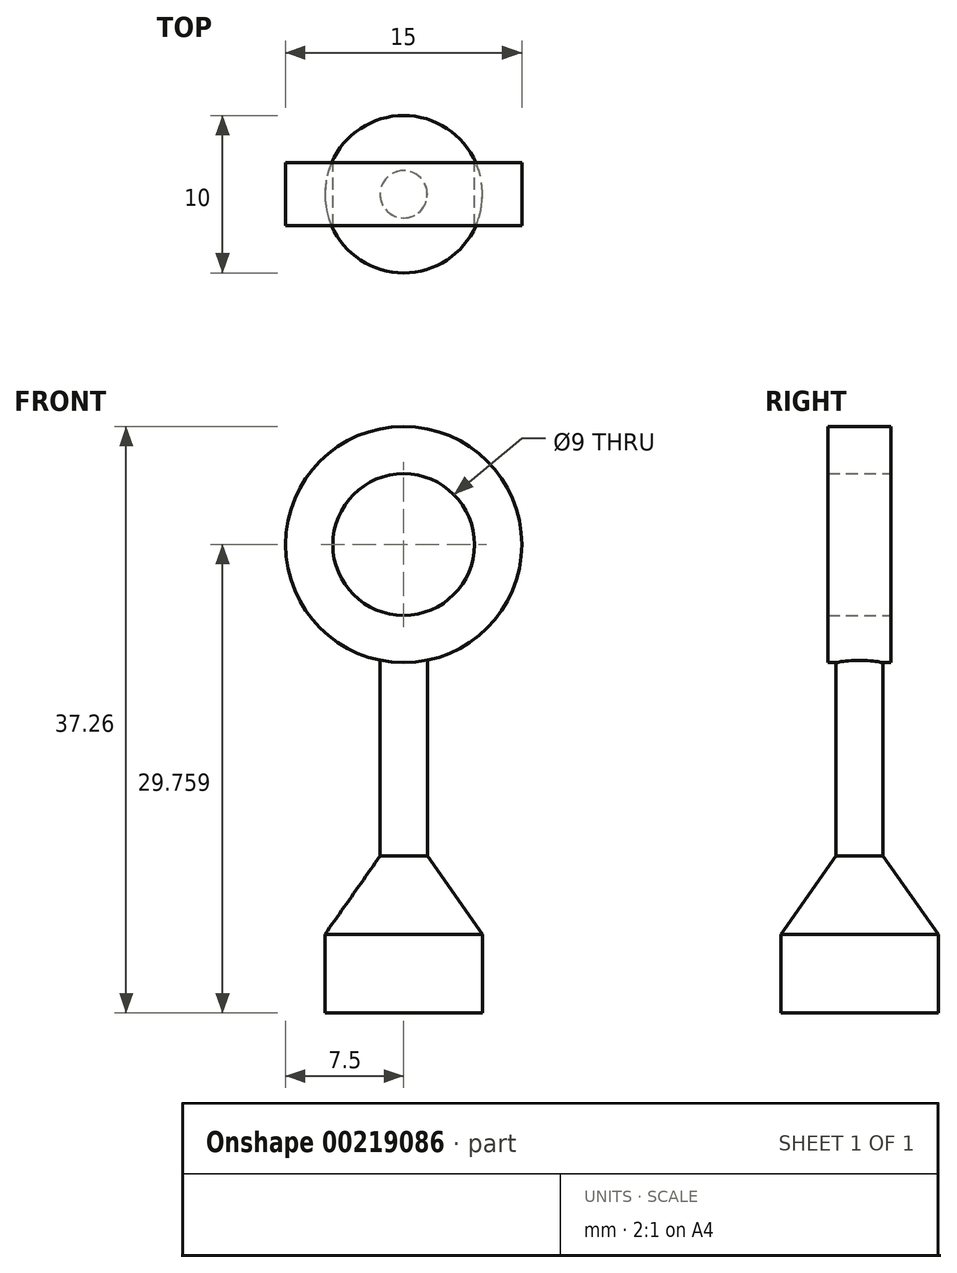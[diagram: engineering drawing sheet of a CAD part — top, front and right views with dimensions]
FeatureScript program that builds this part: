
annotation { "Feature Type Name" : "Feature", "Feature Type Description" : "" }
export const myFeature = defineFeature(function(context is Context, id is Id, definition is map)
    precondition{}
    {
        {
            var Q0;
            Q0=qCreatedBy(makeId("Top.planeOp"),FACE);
            var sketch = newSketch(context, id + "F0", { "sketchPlane" : qUnion([Q0])});
            skCircle(sketch, "E0", {"center": v(0, 0) * mm, "radius": 5 * mm});
            skSolve(sketch);
        }
        {
            var Q0;
            Q0=makeQuery(id+"F0.imprint","IMPRINT",FACE,{"disambiguationData":[TD([[makeQuery(id+"F0.imprint","IMPRINT",EDGE,{"derivedFrom":sQuery(id+"F0.wireOp",EDGE,"E0")}),1.0]])]});
            extrude(context, id + "F1", {"entities" : qUnion([Q0]), "depth" : 5 * mm});
        }
        {
            var Q0;
            Q0=makeQuery(id+"F1.opExtrude","CAP_FACE",FACE,{"disambiguationData":[OSD([sQuery(id+"F0.wireOp",EDGE,"E0")])],"isStart":false});
            var sketch = newSketch(context, id + "F2", { "sketchPlane" : qUnion([Q0])});
            skCircle(sketch, "E1", {"center": v(0, 0) * mm, "radius": 1.5 * mm});
            skSolve(sketch);
        }
        {
            var Q0;
            Q0=qCreatedBy(makeId("Front.planeOp"),FACE);
            var sketch = newSketch(context, id + "F3", { "sketchPlane" : qUnion([Q0])});
            skCircle(sketch, "E2", {"center": v(0, 29.76) * mm, "radius": 7.5 * mm});
            skCircle(sketch, "E3.0", {"center": v(0, 29.76) * mm, "radius": 4.5 * mm});
            skLineSegment(sketch, "E4", {"start": v(0, 12.11) * mm, "end": v(5, 5) * mm});
            skLineSegment(sketch, "E5", {"start": v(0, 12.11) * mm, "end": v(0, 5) * mm});
            skLineSegment(sketch, "E6", {"start": v(5, 5) * mm, "end": v(0, 5) * mm});
            skSolve(sketch);
        }
        {
            var Q0;
            Q0=makeQuery(id+"F2.imprint","IMPRINT",FACE,{"disambiguationData":[TD([[makeQuery(id+"F2.imprint","IMPRINT",EDGE,{"derivedFrom":sQuery(id+"F2.wireOp",EDGE,"E1")}),1.0]])]});
            extrude(context, id + "F4", {"entities" : qUnion([Q0]), "operationType" : NewBodyOperationType.ADD, "depth" : 20 * mm});
        }
        {
            var Q0;
            Q0=makeQuery(id+"F3.imprint","IMPRINT",FACE,{"disambiguationData":[TD([[makeQuery(id+"F3.imprint","IMPRINT",EDGE,{"derivedFrom":sQuery(id+"F3.wireOp",EDGE,"E2")}),1.0]])]});
            extrude(context, id + "F5", {"entities" : qUnion([Q0]), "operationType" : NewBodyOperationType.ADD, "endBound" : BoundingType.SYMMETRIC, "depth" : 4 * mm});
        }
        {
            var Q0;
            Q0=makeQuery(id+"F3.imprint","IMPRINT",FACE,{"disambiguationData":[TD([[makeQuery(id+"F3.imprint","IMPRINT",EDGE,{"derivedFrom":sQuery(id+"F3.wireOp",EDGE,"E4")}),-1.0]])]});
            var Q1;
            Q1=sQuery(id+"F3.wireOp",EDGE,"E5");
            revolve(context, id + "F6", {"operationType" : NewBodyOperationType.ADD, "entities" : qUnion([Q0]), "axis" : qUnion([Q1]), "revolveType" : RevolveType.FULL});
        }
    });
